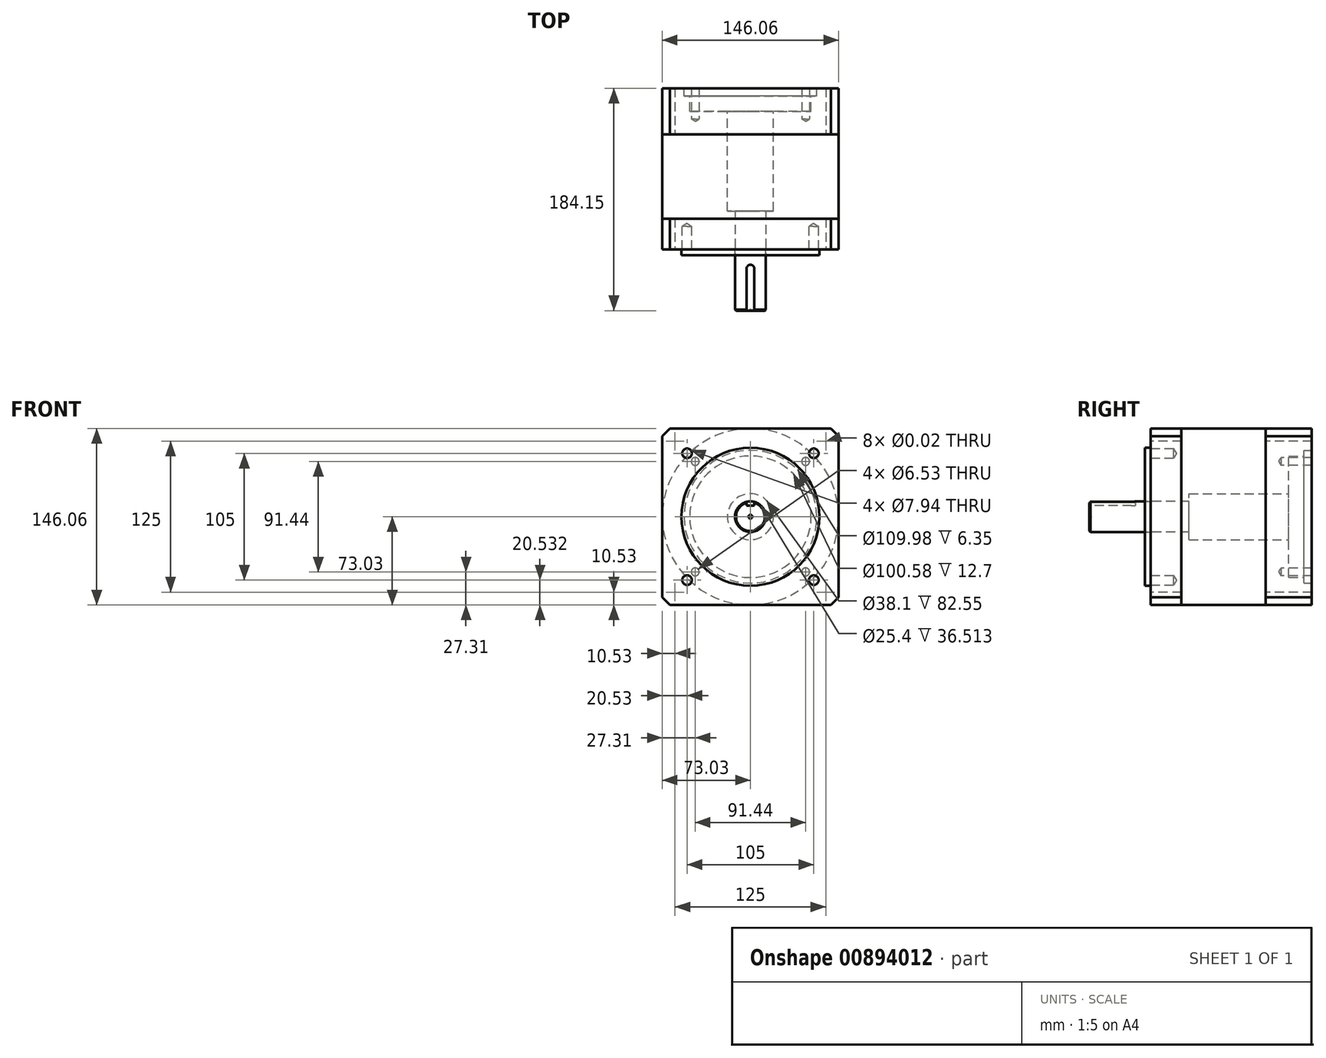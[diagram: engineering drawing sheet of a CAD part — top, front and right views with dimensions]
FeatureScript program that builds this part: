
annotation { "Feature Type Name" : "Feature", "Feature Type Description" : "" }
export const myFeature = defineFeature(function(context is Context, id is Id, definition is map)
    precondition{}
    {
        {
            var Q0;
            Q0=qCreatedBy(makeId("Front.planeOp"),FACE);
            var sketch = newSketch(context, id + "F0", { "sketchPlane" : qUnion([Q0])});
            skLineSegment(sketch, "E0.bottom", {"start": v(-73.02, 73.03) * mm, "end": v(73.03, 73.03) * mm});
            skLineSegment(sketch, "E0.top", {"start": v(-73.03, -73.03) * mm, "end": v(73.03, -73.03) * mm});
            skLineSegment(sketch, "E0.left", {"start": v(-73.02, 73.03) * mm, "end": v(-73.03, -73.03) * mm});
            skLineSegment(sketch, "E0.right", {"start": v(73.03, 73.03) * mm, "end": v(73.03, -73.03) * mm});
            skPoint(sketch, "E0.middle", {"position": v(0, 0) * mm});
            skPoint(sketch, "E1", {"position": v(62.5, 62.5) * mm});
            skPoint(sketch, "E2", {"position": v(-62.5, 62.5) * mm});
            skPoint(sketch, "E3", {"position": v(-62.5, -62.5) * mm});
            skPoint(sketch, "E4", {"position": v(62.5, -62.5) * mm});
            skSolve(sketch);
        }
        {
            var Q0;
            Q0 = qSketchRegion(id + "F0", true);
            extrude(context, id + "F1", {"entities" : qUnion([Q0]), "depth" : 133.35 * mm, "offsetDistance" : 25.4 * mm});
        }
        {
            var Q0;
            Q0=makeQuery(id+"F1.opExtrude","CAP_FACE",FACE,{"disambiguationData":[OSD([sQuery(id+"F0.wireOp",EDGE,"E0.bottom"),sQuery(id+"F0.wireOp",EDGE,"E0.top"),sQuery(id+"F0.wireOp",EDGE,"E0.left"),sQuery(id+"F0.wireOp",EDGE,"E0.right")])],"isStart":true});
            extrude(context, id + "F2", {"entities" : qUnion([Q0]), "operationType" : NewBodyOperationType.REMOVE, "oppositeDirection" : true, "depth" : 107.95 * mm, "offsetDistance" : 25.4 * mm});
        }
        {
            var Q0;
            Q0=makeQuery(id+"F0.imprint","IMPRINT",FACE,{"disambiguationData":[TD([[makeQuery(id+"F0.imprint","IMPRINT",EDGE,{"derivedFrom":sQuery(id+"F0.wireOp",EDGE,"E0.bottom")}),-1.0]])]});
            extrude(context, id + "F3", {"entities" : qUnion([Q0]), "depth" : 38.1 * mm, "offsetDistance" : 25.4 * mm});
        }
        {
            var Q0;
            Q0=makeQuery(id+"F0.imprint","IMPRINT",FACE,{"disambiguationData":[TD([[makeQuery(id+"F0.imprint","IMPRINT",EDGE,{"derivedFrom":sQuery(id+"F0.wireOp",EDGE,"E0.bottom")}),-1.0]])]});
            var sketch = newSketch(context, id + "F4", { "sketchPlane" : qUnion([Q0])});
            skCircle(sketch, "E5", {"center": v(0, 0) * mm, "radius": 73.03 * mm});
            skSolve(sketch);
        }
        {
            var Q0;
            Q0 = qSketchRegion(id + "F4", true);
            var Q1;
            Q1=makeQuery(id+"F1.opExtrude","CAP_FACE",FACE,{"disambiguationData":[OSD([sQuery(id+"F0.wireOp",EDGE,"E0.bottom"),sQuery(id+"F0.wireOp",EDGE,"E0.top"),sQuery(id+"F0.wireOp",EDGE,"E0.left"),sQuery(id+"F0.wireOp",EDGE,"E0.right")])],"isStart":false});
            extrude(context, id + "F5", {"entities" : qUnion([Q0]), "operationType" : NewBodyOperationType.ADD, "endBound" : BoundingType.UP_TO_SURFACE, "depth" : 127 * mm, "endBoundEntityFace" : qUnion([Q1]), "offsetDistance" : 25.4 * mm});
        }
        {
            var Q0;
            Q0=sQuery(id+"F0.wireOp",VERTEX,"E1");
            var Q1;
            Q1=sQuery(id+"F0.wireOp",VERTEX,"E2");
            var Q2;
            Q2=sQuery(id+"F0.wireOp",VERTEX,"E3");
            var Q3;
            Q3=sQuery(id+"F0.wireOp",VERTEX,"E4");
            var Q4;
            Q4=makeQuery(id+"F1.opExtrude","SWEPT_BODY",BODY,{"disambiguationData":[OSD([sQuery(id+"F0.wireOp",EDGE,"E0.bottom"),sQuery(id+"F0.wireOp",EDGE,"E0.top"),sQuery(id+"F0.wireOp",EDGE,"E0.left"),sQuery(id+"F0.wireOp",EDGE,"E0.right")])]});
            hole(context, id + "F6", {"style" : HoleStyle.SIMPLE, "endStyle" : HoleEndStyle.THROUGH, "oppositeDirection" : true, "standardTappedOrClearance" : lookupTablePath({ "standard" : "ANSI", "size" : "7/16 (0.44)", "type" : "Drilled" }), "standardBlindInLast" : lookupTablePath({ "standard" : "ANSI", "size" : "7/16", "type" : "Drilled" }), "holeDiameter" : 7 / 406.4 * mm, "majorDiameter" : 4.83 * mm, "isTappedThrough" : true, "tappedDepth" : 10.34 * mm, "tapClearance" : 3, "locations" : qUnion([Q0, Q1, Q2, Q3]), "scope" : qUnion([Q4]), "startStyle" : HoleStartStyle.SKETCH});
        }
        {
            var Q0;
            Q0=makeQuery(id+"F0.imprint","IMPRINT",FACE,{"disambiguationData":[TD([[makeQuery(id+"F0.imprint","IMPRINT",EDGE,{"derivedFrom":sQuery(id+"F0.wireOp",EDGE,"E0.bottom")}),-1.0]])]});
            var sketch = newSketch(context, id + "F7", { "sketchPlane" : qUnion([Q0])});
            skPoint(sketch, "E6", {"position": v(45.72, 45.72) * mm});
            skPoint(sketch, "E7", {"position": v(-45.72, 45.72) * mm});
            skPoint(sketch, "E8", {"position": v(-45.72, -45.72) * mm});
            skPoint(sketch, "E9", {"position": v(45.72, -45.72) * mm});
            skCircle(sketch, "E10", {"center": v(0, 0) * mm, "radius": 55 * mm});
            skCircle(sketch, "E11", {"center": v(0, 0) * mm, "radius": 50.3 * mm});
            skCircle(sketch, "E12", {"center": v(0, 0) * mm, "radius": 19.05 * mm});
            skSolve(sketch);
        }
        {
            var Q0;
            Q0=sQuery(id+"F7.wireOp",VERTEX,"E7");
            var Q1;
            Q1=sQuery(id+"F7.wireOp",VERTEX,"E6");
            var Q2;
            Q2=sQuery(id+"F7.wireOp",VERTEX,"E9");
            var Q3;
            Q3=sQuery(id+"F7.wireOp",VERTEX,"E8");
            var Q4;
            Q4=makeQuery(id+"F1.opExtrude","SWEPT_BODY",BODY,{"disambiguationData":[OSD([sQuery(id+"F0.wireOp",EDGE,"E0.bottom"),sQuery(id+"F0.wireOp",EDGE,"E0.top"),sQuery(id+"F0.wireOp",EDGE,"E0.left"),sQuery(id+"F0.wireOp",EDGE,"E0.right")])]});
            hole(context, id + "F8", {"style" : HoleStyle.SIMPLE, "endStyle" : HoleEndStyle.BLIND, "oppositeDirection" : true, "standardTappedOrClearance" : lookupTablePath({ "standard" : "ANSI", "engagement" : "75%", "pitch" : "18 tpi", "size" : "5/16", "type" : "Tapped" }), "standardBlindInLast" : lookupTablePath({ "standard" : "ANSI", "engagement" : "75%", "pitch" : "18 tpi", "size" : "5/16", "type" : "Tapped" }), "holeDiameter" : 6.53 * mm, "majorDiameter" : 7.94 * mm, "showTappedDepth" : true, "holeDepth" : 25.4 * mm, "isTappedThrough" : true, "tappedDepth" : 21.17 * mm, "tapClearance" : 3, "locations" : qUnion([Q0, Q1, Q2, Q3]), "scope" : qUnion([Q4]), "startStyle" : HoleStartStyle.SKETCH});
        }
        {
            var Q0;
            Q0=makeQuery(id+"F7.imprint","IMPRINT",FACE,{"disambiguationData":[TD([[makeQuery(id+"F7.imprint","IMPRINT",EDGE,{"derivedFrom":sQuery(id+"F7.wireOp",EDGE,"E11")}),1.0]])]});
            extrude(context, id + "F9", {"entities" : qUnion([Q0]), "operationType" : NewBodyOperationType.REMOVE, "depth" : 19.05 * mm, "offsetDistance" : 25.4 * mm});
        }
        {
            var Q0;
            Q0=makeQuery(id+"F7.imprint","IMPRINT",FACE,{"disambiguationData":[TD([[makeQuery(id+"F7.imprint","IMPRINT",EDGE,{"derivedFrom":sQuery(id+"F7.wireOp",EDGE,"E10")}),1.0]])]});
            extrude(context, id + "F10", {"entities" : qUnion([Q0]), "operationType" : NewBodyOperationType.REMOVE, "depth" : 6.35 * mm, "offsetDistance" : 25.4 * mm});
        }
        {
            var Q0;
            Q0=makeQuery(id+"F7.imprint","IMPRINT",FACE,{"disambiguationData":[TD([[makeQuery(id+"F7.imprint","IMPRINT",EDGE,{"derivedFrom":sQuery(id+"F7.wireOp",EDGE,"E12")}),1.0]])]});
            extrude(context, id + "F11", {"entities" : qUnion([Q0]), "operationType" : NewBodyOperationType.REMOVE, "depth" : 101.6 * mm, "offsetDistance" : 25.4 * mm});
        }
        {
            var Q0;
            Q0=makeQuery(id+"F1.opExtrude","CAP_FACE",FACE,{"disambiguationData":[OSD([sQuery(id+"F0.wireOp",EDGE,"E0.bottom"),sQuery(id+"F0.wireOp",EDGE,"E0.top"),sQuery(id+"F0.wireOp",EDGE,"E0.left"),sQuery(id+"F0.wireOp",EDGE,"E0.right")])],"isStart":false});
            var sketch = newSketch(context, id + "F12", { "sketchPlane" : qUnion([Q0])});
            skCircle(sketch, "E13", {"center": v(0, 0) * mm, "radius": 57.15 * mm});
            skCircle(sketch, "E14", {"center": v(0, 0) * mm, "radius": 12.7 * mm});
            skPoint(sketch, "E15", {"position": v(52.5, 52.5) * mm});
            skPoint(sketch, "E16", {"position": v(-52.5, 52.5) * mm});
            skPoint(sketch, "E17", {"position": v(-52.5, -52.5) * mm});
            skPoint(sketch, "E18", {"position": v(52.5, -52.5) * mm});
            skSolve(sketch);
        }
        {
            var Q0;
            Q0=makeQuery(id+"F12.imprint","IMPRINT",FACE,{"disambiguationData":[TD([[makeQuery(id+"F12.imprint","IMPRINT",EDGE,{"derivedFrom":sQuery(id+"F12.wireOp",EDGE,"E14")}),1.0]])]});
            extrude(context, id + "F13", {"entities" : qUnion([Q0]), "operationType" : NewBodyOperationType.REMOVE, "endBound" : BoundingType.THROUGH_ALL, "oppositeDirection" : true, "depth" : 25.4 * mm, "offsetDistance" : 25.4 * mm});
        }
        {
            var Q0;
            Q0=makeQuery(id+"F12.imprint","IMPRINT",FACE,{"disambiguationData":[TD([[makeQuery(id+"F12.imprint","IMPRINT",EDGE,{"derivedFrom":sQuery(id+"F12.wireOp",EDGE,"E13")}),1.0]])]});
            extrude(context, id + "F14", {"entities" : qUnion([Q0]), "operationType" : NewBodyOperationType.ADD, "depth" : 4.76 * mm, "offsetDistance" : 25.4 * mm});
        }
        {
            var Q0;
            Q0=sQuery(id+"F12.wireOp",VERTEX,"E15");
            var Q1;
            Q1=sQuery(id+"F12.wireOp",VERTEX,"E18");
            var Q2;
            Q2=sQuery(id+"F12.wireOp",VERTEX,"E17");
            var Q3;
            Q3=sQuery(id+"F12.wireOp",VERTEX,"E16");
            var Q4;
            Q4=makeQuery(id+"F1.opExtrude","SWEPT_BODY",BODY,{"disambiguationData":[OSD([sQuery(id+"F0.wireOp",EDGE,"E0.bottom"),sQuery(id+"F0.wireOp",EDGE,"E0.top"),sQuery(id+"F0.wireOp",EDGE,"E0.left"),sQuery(id+"F0.wireOp",EDGE,"E0.right")])]});
            hole(context, id + "F15", {"style" : HoleStyle.SIMPLE, "endStyle" : HoleEndStyle.BLIND, "standardTappedOrClearance" : lookupTablePath({ "standard" : "ANSI", "engagement" : "75%", "pitch" : "16 tpi", "size" : "3/8", "type" : "Tapped" }), "standardBlindInLast" : lookupTablePath({ "standard" : "ANSI", "engagement" : "75%", "pitch" : "16 tpi", "size" : "3/8", "type" : "Tapped" }), "holeDiameter" : 7.94 * mm, "majorDiameter" : 9.52 * mm, "showTappedDepth" : true, "holeDepth" : 19.05 * mm, "isTappedThrough" : true, "tappedDepth" : 14.29 * mm, "tapClearance" : 3, "locations" : qUnion([Q0, Q1, Q2, Q3]), "scope" : qUnion([Q4]), "startStyle" : HoleStartStyle.SKETCH});
        }
        {
            var Q0;
            Q0=makeQuery(id+"F1.opExtrude","SWEPT_EDGE",EDGE,{"disambiguationData":[OSD([sQuery(id+"F0.wireOp",EDGE,"E0.bottom"),sQuery(id+"F0.wireOp",EDGE,"E0.right")])]});
            var Q1;
            Q1=makeQuery(id+"F1.opExtrude","SWEPT_EDGE",EDGE,{"disambiguationData":[OSD([sQuery(id+"F0.wireOp",EDGE,"E0.top"),sQuery(id+"F0.wireOp",EDGE,"E0.right")])]});
            var Q2;
            Q2=makeQuery(id+"F1.opExtrude","SWEPT_EDGE",EDGE,{"disambiguationData":[OSD([sQuery(id+"F0.wireOp",EDGE,"E0.top"),sQuery(id+"F0.wireOp",EDGE,"E0.left")])]});
            var Q3;
            Q3=makeQuery(id+"F1.opExtrude","SWEPT_EDGE",EDGE,{"disambiguationData":[OSD([sQuery(id+"F0.wireOp",EDGE,"E0.bottom"),sQuery(id+"F0.wireOp",EDGE,"E0.left")])]});
            var Q4;
            Q4=makeQuery(id+"F3.opExtrude","SWEPT_EDGE",EDGE,{"disambiguationData":[OSD([sQuery(id+"F0.wireOp",EDGE,"E0.top"),sQuery(id+"F0.wireOp",EDGE,"E0.left")])]});
            var Q5;
            Q5=makeQuery(id+"F3.opExtrude","SWEPT_EDGE",EDGE,{"disambiguationData":[OSD([sQuery(id+"F0.wireOp",EDGE,"E0.bottom"),sQuery(id+"F0.wireOp",EDGE,"E0.left")])]});
            var Q6;
            Q6=makeQuery(id+"F3.opExtrude","SWEPT_EDGE",EDGE,{"disambiguationData":[OSD([sQuery(id+"F0.wireOp",EDGE,"E0.bottom"),sQuery(id+"F0.wireOp",EDGE,"E0.right")])]});
            var Q7;
            Q7=makeQuery(id+"F3.opExtrude","SWEPT_EDGE",EDGE,{"disambiguationData":[OSD([sQuery(id+"F0.wireOp",EDGE,"E0.top"),sQuery(id+"F0.wireOp",EDGE,"E0.right")])]});
            chamfer(context, id + "F16", {"entities" : qUnion([Q0, Q1, Q2, Q3, Q4, Q5, Q6, Q7]), "width" : 6.35 * mm, "tangentPropagation" : true});
        }
        {
            var Q0;
            Q0=makeQuery(id+"F12.imprint","IMPRINT",FACE,{"disambiguationData":[TD([[makeQuery(id+"F12.imprint","IMPRINT",EDGE,{"derivedFrom":sQuery(id+"F12.wireOp",EDGE,"E14")}),1.0]])]});
            extrude(context, id + "F17", {"entities" : qUnion([Q0]), "depth" : 50.8 * mm, "offsetDistance" : 25.4 * mm});
        }
        {
            var Q0;
            Q0=makeQuery(id+"F17.opExtrude","CAP_FACE",FACE,{"disambiguationData":[OSD([sQuery(id+"F12.wireOp",EDGE,"E14")])],"isStart":false});
            var sketch = newSketch(context, id + "F18", { "sketchPlane" : qUnion([Q0])});
            skLineSegment(sketch, "E19", {"start": v(0, 0) * mm, "end": v(0, 12.7) * mm, "construction": true});
            skLineSegment(sketch, "E20", {"start": v(0, 9.12) * mm, "end": v(-3.18, 9.12) * mm});
            skLineSegment(sketch, "E21", {"start": v(0, 9.12) * mm, "end": v(3.18, 9.12) * mm});
            skLineSegment(sketch, "E22", {"start": v(-3.18, 9.12) * mm, "end": v(-3.18, 12.3) * mm});
            skLineSegment(sketch, "E23", {"start": v(3.18, 9.12) * mm, "end": v(3.18, 12.3) * mm});
            skCircle(sketch, "E24", {"center": v(0, 0) * mm, "radius": 1.59 * mm});
            skSolve(sketch);
        }
        {
            var Q0;
            Q0=makeQuery(id+"F18.imprint","IMPRINT",FACE,{"disambiguationData":[TD([[makeQuery(id+"F18.imprint","IMPRINT",EDGE,{"derivedFrom":sQuery(id+"F18.wireOp",EDGE,"E20")}),-1.0]])]});
            extrude(context, id + "F19", {"entities" : qUnion([Q0]), "operationType" : NewBodyOperationType.REMOVE, "oppositeDirection" : true, "depth" : 38.1 * mm, "offsetDistance" : 25.4 * mm});
        }
        {
            var Q0;
            Q0=makeQuery(id+"F19.boolean.opBoolean","COPY",EDGE,{"derivedFrom":makeQuery(id+"F19.opExtrude","CAP_EDGE",EDGE,{"disambiguationData":[OSD([sQuery(id+"F18.wireOp",EDGE,"E22")])],"isStart":false})});
            var Q1;
            Q1=makeQuery(id+"F19.boolean.opBoolean","COPY",EDGE,{"derivedFrom":makeQuery(id+"F19.opExtrude","CAP_EDGE",EDGE,{"disambiguationData":[OSD([sQuery(id+"F18.wireOp",EDGE,"E23")])],"isStart":false})});
            fillet(context, id + "F20", {"entities" : qUnion([Q0, Q1]), "radius" : 3.17 * mm, "tangentPropagation" : true, "allowEdgeOverflow" : false});
        }
        {
            var Q0;
            Q0=makeQuery(id+"F18.imprint","IMPRINT",FACE,{"disambiguationData":[TD([[makeQuery(id+"F18.imprint","IMPRINT",EDGE,{"derivedFrom":sQuery(id+"F18.wireOp",EDGE,"E24")}),1.0]])]});
            extrude(context, id + "F21", {"entities" : qUnion([Q0]), "operationType" : NewBodyOperationType.REMOVE, "oppositeDirection" : true, "depth" : 1.59 * mm, "offsetDistance" : 25.4 * mm});
        }
        {
            var Q0;
            Q0=makeQuery(id+"F21.boolean.opBoolean","COPY",EDGE,{"derivedFrom":makeQuery(id+"F21.opExtrude","CAP_EDGE",EDGE,{"disambiguationData":[OSD([sQuery(id+"F18.wireOp",EDGE,"E24")])],"isStart":false})});
            chamfer(context, id + "F22", {"entities" : qUnion([Q0]), "width" : 1.59 * mm, "tangentPropagation" : true});
        }
        {
            var Q0;
            Q0=makeQuery(id+"F17.opExtrude","CAP_EDGE",EDGE,{"disambiguationData":[OSD([sQuery(id+"F12.wireOp",EDGE,"E14")])],"isStart":false});
            chamfer(context, id + "F23", {"entities" : qUnion([Q0]), "width" : 0.8 * mm, "tangentPropagation" : true});
        }
    });
